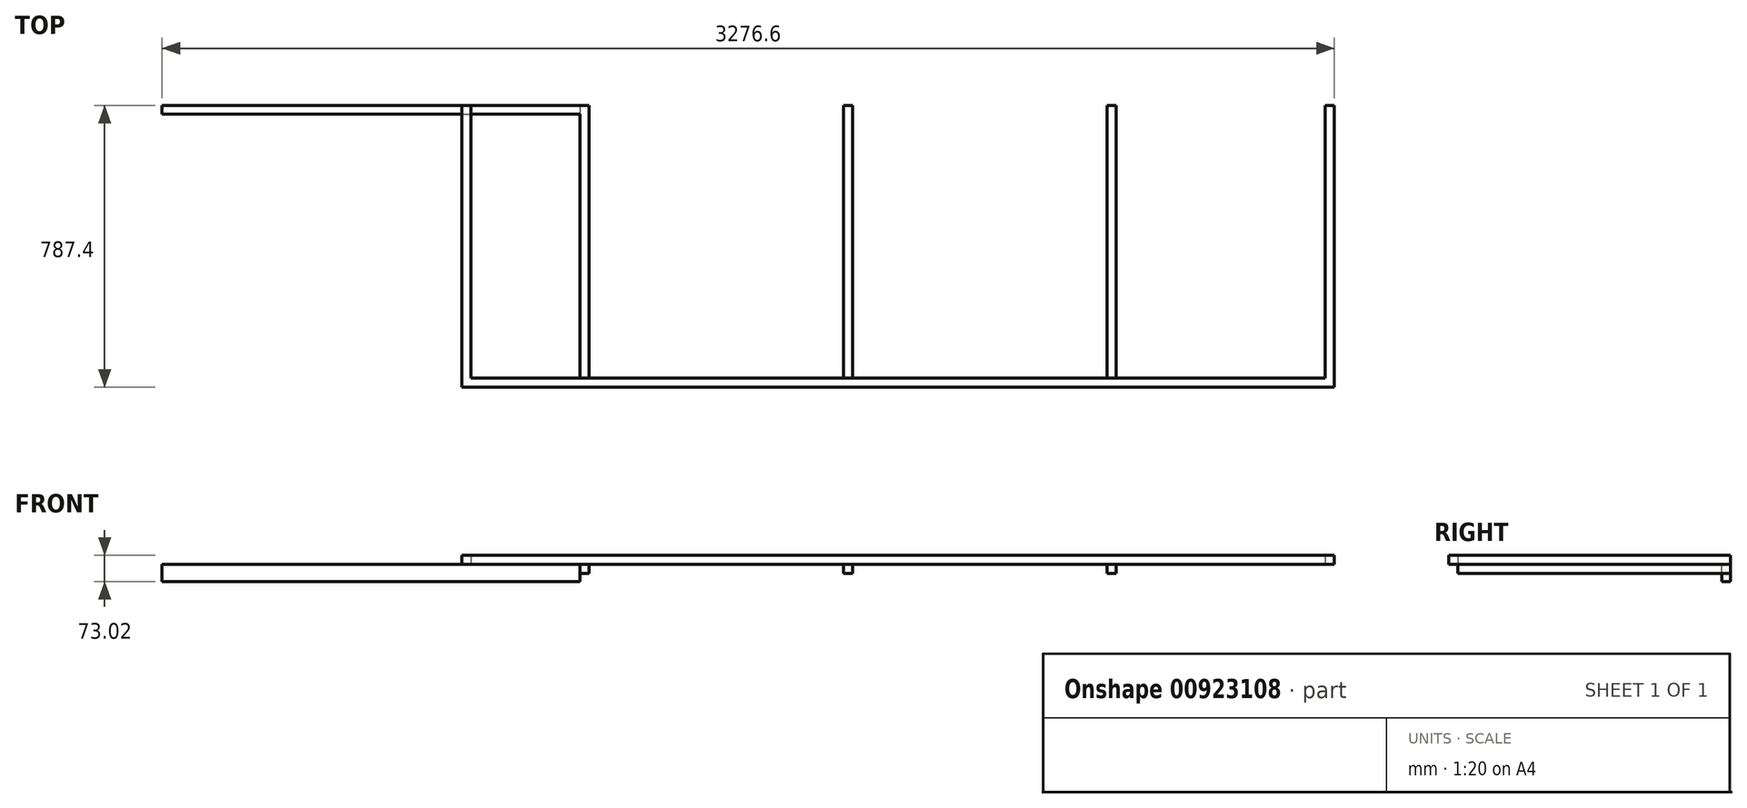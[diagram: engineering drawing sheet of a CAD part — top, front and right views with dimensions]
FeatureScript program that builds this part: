
annotation { "Feature Type Name" : "Feature", "Feature Type Description" : "" }
export const myFeature = defineFeature(function(context is Context, id is Id, definition is map)
    precondition{}
    {
        {
            var Q0;
            Q0=qCreatedBy(makeId("Top.planeOp"),FACE);
            var sketch = newSketch(context, id + "F0", { "sketchPlane" : qUnion([Q0])});
            skLineSegment(sketch, "E0.bottom", {"start": v(1252.4, -787.4) * mm, "end": v(-1186, -787.4) * mm});
            skLineSegment(sketch, "E0.top", {"start": v(1252.4, -762) * mm, "end": v(-1186, -762) * mm});
            skLineSegment(sketch, "E0.left", {"start": v(1252.4, -787.4) * mm, "end": v(1252.4, -762) * mm});
            skLineSegment(sketch, "E0.right", {"start": v(-1186, -787.4) * mm, "end": v(-1186, -762) * mm});
            skLineSegment(sketch, "E1.bottom", {"start": v(1252.4, -762) * mm, "end": v(1227, -762) * mm});
            skLineSegment(sketch, "E1.top", {"start": v(1252.4, 0) * mm, "end": v(1227, 0) * mm});
            skLineSegment(sketch, "E1.left", {"start": v(1252.4, -762) * mm, "end": v(1252.4, 0) * mm});
            skLineSegment(sketch, "E1.right", {"start": v(1227, -762) * mm, "end": v(1227, 0) * mm});
            skLineSegment(sketch, "E2.bottom", {"start": v(-1186, -762) * mm, "end": v(-1160.6, -762) * mm});
            skLineSegment(sketch, "E2.top", {"start": v(-1186, 0) * mm, "end": v(-1160.6, 0) * mm});
            skLineSegment(sketch, "E2.left", {"start": v(-1186, -762) * mm, "end": v(-1186, 0) * mm});
            skLineSegment(sketch, "E2.right", {"start": v(-1160.6, -762) * mm, "end": v(-1160.6, 0) * mm});
            skSolve(sketch);
        }
        {
            var Q0;
            Q0 = qSketchRegion(id + "F0", true);
            extrude(context, id + "F1", {"entities" : qUnion([Q0]), "depth" : 25.4 * mm, "offsetDistance" : 25.4 * mm});
        }
        {
            var Q0;
            Q0=qCreatedBy(makeId("Top.planeOp"),FACE);
            var sketch = newSketch(context, id + "F2", { "sketchPlane" : qUnion([Q0])});
            skLineSegment(sketch, "E3.bottom", {"start": v(-2024.2, 0) * mm, "end": v(-855.8, 0) * mm});
            skLineSegment(sketch, "E3.top", {"start": v(-2024.2, -23.81) * mm, "end": v(-855.8, -23.81) * mm});
            skLineSegment(sketch, "E3.left", {"start": v(-2024.2, 0) * mm, "end": v(-2024.2, -23.81) * mm});
            skLineSegment(sketch, "E3.right", {"start": v(-855.8, 0) * mm, "end": v(-855.8, -23.81) * mm});
            skLineSegment(sketch, "E4.top", {"start": v(-855.8, -762) * mm, "end": v(-830.4, -762) * mm});
            skSolve(sketch);
        }
        {
            var Q0;
            Q0 = qSketchRegion(id + "F2", true);
            extrude(context, id + "F3", {"entities" : qUnion([Q0]), "operationType" : NewBodyOperationType.ADD, "oppositeDirection" : true, "depth" : 47.62 * mm, "offsetDistance" : 25.4 * mm});
        }
        {
            var Q0;
            Q0=qCreatedBy(makeId("Top.planeOp"),FACE);
            var sketch = newSketch(context, id + "F4", { "sketchPlane" : qUnion([Q0])});
            skLineSegment(sketch, "E5.bottom", {"start": v(-855.8, 0) * mm, "end": v(-830.4, 0) * mm});
            skLineSegment(sketch, "E5.right", {"start": v(-830.4, 0) * mm, "end": v(-830.4, -762) * mm});
            skLineSegment(sketch, "E6.bottom", {"start": v(-119.2, 0) * mm, "end": v(-93.8, 0) * mm});
            skLineSegment(sketch, "E6.top", {"start": v(-119.2, -762) * mm, "end": v(-93.8, -762) * mm});
            skLineSegment(sketch, "E6.left", {"start": v(-119.2, 0) * mm, "end": v(-119.2, -762) * mm});
            skLineSegment(sketch, "E6.right", {"start": v(-93.8, 0) * mm, "end": v(-93.8, -762) * mm});
            skLineSegment(sketch, "E7.bottom", {"start": v(617.4, 0) * mm, "end": v(642.8, 0) * mm});
            skLineSegment(sketch, "E7.top", {"start": v(617.4, -762) * mm, "end": v(642.8, -762) * mm});
            skLineSegment(sketch, "E7.left", {"start": v(617.4, 0) * mm, "end": v(617.4, -762) * mm});
            skLineSegment(sketch, "E7.right", {"start": v(642.8, 0) * mm, "end": v(642.8, -762) * mm});
            skLineSegment(sketch, "E8.bottom", {"start": v(1226.6, 0) * mm, "end": v(1252, 0) * mm});
            skLineSegment(sketch, "E8.top", {"start": v(1226.6, -762) * mm, "end": v(1252, -762) * mm});
            skLineSegment(sketch, "E8.left", {"start": v(1226.6, 0) * mm, "end": v(1226.6, -762) * mm});
            skLineSegment(sketch, "E8.right", {"start": v(1252, 0) * mm, "end": v(1252, -762) * mm});
            skLineSegment(sketch, "E9", {"start": v(-855.8, 0) * mm, "end": v(-855.8, -762.14) * mm});
            skLineSegment(sketch, "E10", {"start": v(-830.4, -762) * mm, "end": v(-855.8, -762.14) * mm});
            skSolve(sketch);
        }
        {
            var Q0;
            Q0=makeQuery(id+"F4.imprint","IMPRINT",FACE,{"disambiguationData":[TD([[makeQuery(id+"F4.imprint","IMPRINT",EDGE,{"derivedFrom":sQuery(id+"F4.wireOp",EDGE,"E6.bottom")}),-1.0]])]});
            var Q1;
            Q1=makeQuery(id+"F4.imprint","IMPRINT",FACE,{"disambiguationData":[TD([[makeQuery(id+"F4.imprint","IMPRINT",EDGE,{"derivedFrom":sQuery(id+"F4.wireOp",EDGE,"E7.bottom")}),-1.0]])]});
            var Q2;
            Q2=makeQuery(id+"F4.imprint","IMPRINT",FACE,{"disambiguationData":[TD([[makeQuery(id+"F4.imprint","IMPRINT",EDGE,{"derivedFrom":sQuery(id+"F4.wireOp",EDGE,"E5.bottom")}),-1.0]])]});
            extrude(context, id + "F5", {"entities" : qUnion([Q0, Q1, Q2]), "operationType" : NewBodyOperationType.ADD, "oppositeDirection" : true, "depth" : 25.4 * mm, "offsetDistance" : 25.4 * mm});
        }
    });
